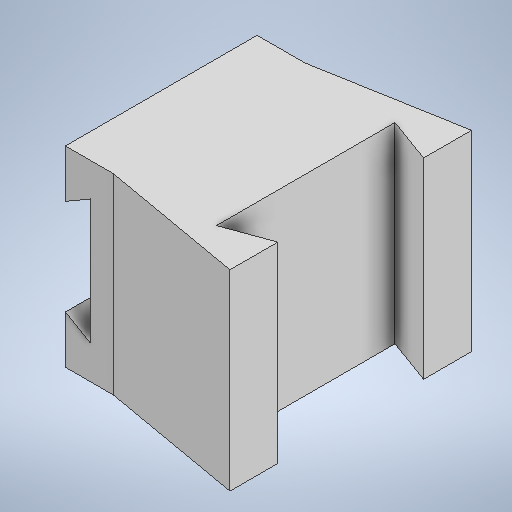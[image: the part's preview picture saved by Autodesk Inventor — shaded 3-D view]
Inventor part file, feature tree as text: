
AUTODESK INVENTOR PART (.ipt)
format: ipt  version: 2025.2 (Build 292293000, 293)  size: 213,504 bytes
history: native  units: mm
features: extrude x3, sketch x3
ambient origin geometry x8: Origin, YZ Plane, XZ Plane, XY Plane, X Axis, Y Axis, Z Axis, Center Point
bodies: Solid1 (feature_tree)
feature tree (6):
  extrude  "Extrusion1"  Depth=15.0mm
  extrude  "Extrusion2"  Depth=5.0mm
  extrude  "Extrusion3"  Depth=20.0mm
  sketch  "Sketch1"  dims[d0=20.0mm d1=15.0mm]
  sketch  "Sketch2"  dims[d2=17.453293mm d3=5.0mm]
  sketch  "Sketch3"  dims[d4=5.0mm d5=12.217305mm d6=15.0mm d7=5.0mm d8=5.0mm d9=20.0mm d10=0.0mm d11=5.0mm d12=0.0mm d13=5.0mm d14=5.0mm d15=3.0mm d16=150.0deg d17=3.0mm d18=50.0mm d19=0.0mm]
